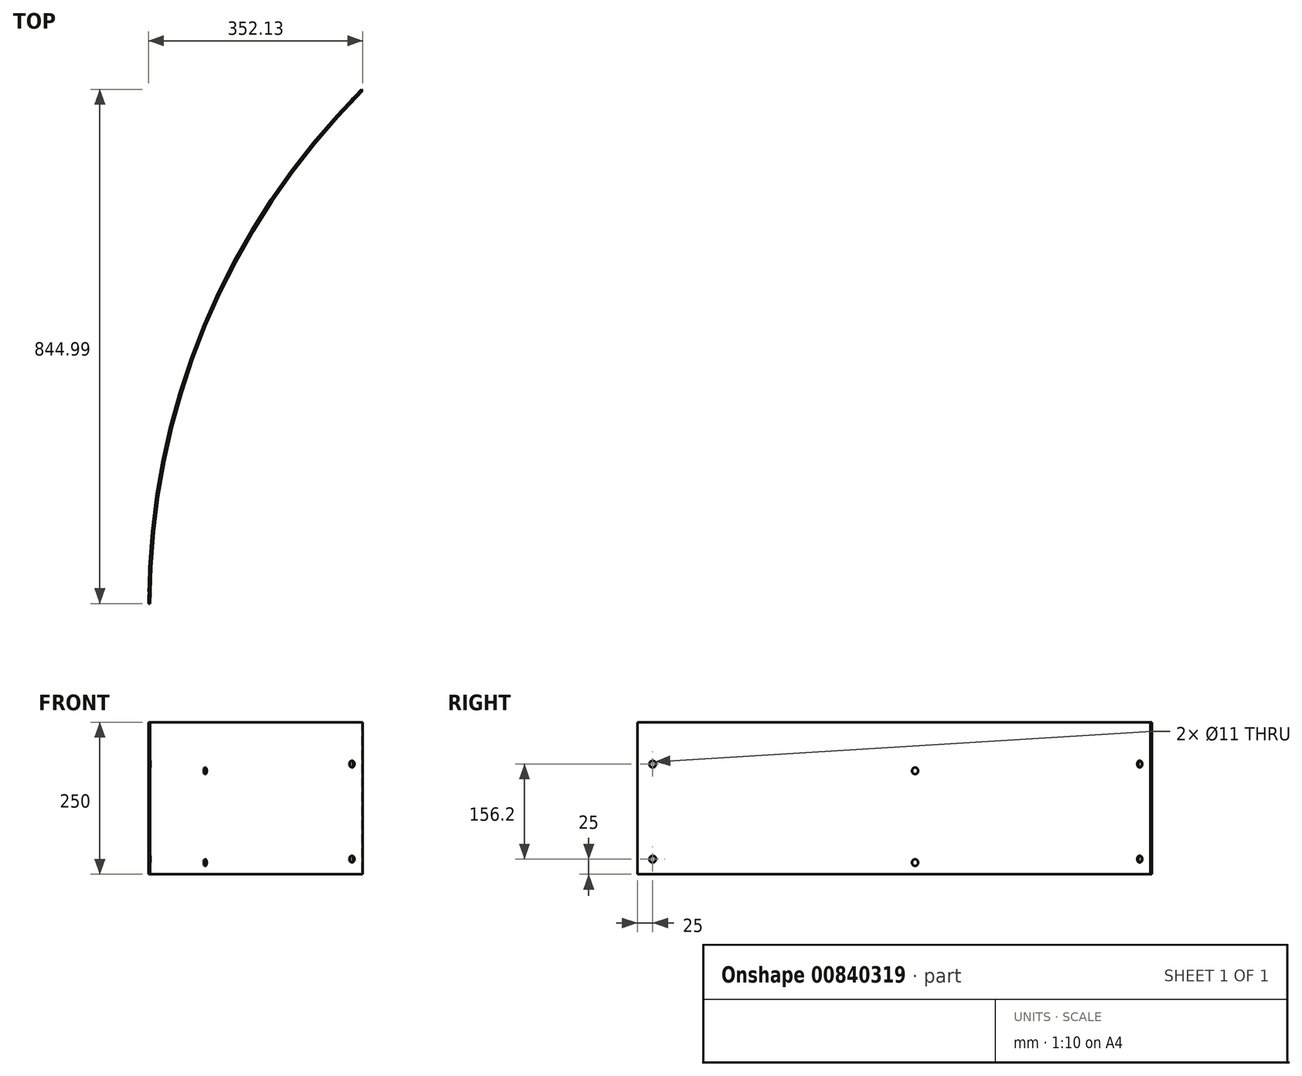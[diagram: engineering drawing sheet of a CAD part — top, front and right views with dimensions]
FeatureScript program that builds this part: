
annotation { "Feature Type Name" : "Feature", "Feature Type Description" : "" }
export const myFeature = defineFeature(function(context is Context, id is Id, definition is map)
    precondition{}
    {
        {
            var Q0;
            Q0=qCreatedBy(makeId("Top.planeOp"),FACE);
            var sketch = newSketch(context, id + "F0", { "sketchPlane" : qUnion([Q0])});
            skArc(sketch, "E0", {"start": v(349.13, 842.87) * mm, "mid": v(90.74, 456.16) * mm, "end": v(0, 0) * mm});
            skLineSegment(sketch, "E1", {"start": v(0, 0) * mm, "end": v(1192, 0) * mm, "construction": true});
            skLineSegment(sketch, "E2", {"start": v(1192, 0) * mm, "end": v(349.13, 842.87) * mm, "construction": true});
            skSolve(sketch);
        }
        {
            var Q0;
            Q0=qCreatedBy(makeId("Front.planeOp"),FACE);
            var sketch = newSketch(context, id + "F1", { "sketchPlane" : qUnion([Q0])});
            skLineSegment(sketch, "E3.bottom", {"start": v(0, 125) * mm, "end": v(-3, 125) * mm});
            skLineSegment(sketch, "E3.top", {"start": v(0, -125) * mm, "end": v(-3, -125) * mm});
            skLineSegment(sketch, "E3.left", {"start": v(0, 125) * mm, "end": v(0, -125) * mm});
            skLineSegment(sketch, "E3.right", {"start": v(-3, 125) * mm, "end": v(-3, -125) * mm});
            skSolve(sketch);
        }
        {
            var Q0;
            Q0=makeQuery(id+"F1.imprint","IMPRINT",FACE,{"disambiguationData":[TD([[makeQuery(id+"F1.imprint","IMPRINT",EDGE,{"derivedFrom":sQuery(id+"F1.wireOp",EDGE,"E3.bottom")}),1.0]])]});
            var Q1;
            Q1=sQuery(id+"F0.wireOp",EDGE,"A1xx75fL-8SPs-Z9ri-CPTb-JmtdQX2gj51n");
            var Q2;
            Q2=sQuery(id+"F0.wireOp",EDGE,"E0");
            var Q3;
            Q3=sQuery(id+"F0.wireOp",EDGE,"6DeDyjJt-B3l9-2hQ4-MW4A-s2AXSr22zXWG");
            sweep(context, id + "F2", {"profiles" : qUnion([Q0]), "path" : qUnion([Q1, Q2, Q3])});
        }
        {
            var Q0;
            Q0=qCreatedBy(makeId("Right.planeOp"),FACE);
            var sketch = newSketch(context, id + "F3", { "sketchPlane" : qUnion([Q0])});
            skPoint(sketch, "E4", {"position": v(25, -100) * mm});
            skPoint(sketch, "E5", {"position": v(25, 56.2) * mm});
            skCircle(sketch, "E6", {"center": v(25, 56.2) * mm, "radius": 5.5 * mm});
            skCircle(sketch, "E7", {"center": v(25, -100) * mm, "radius": 5.5 * mm});
            skSolve(sketch);
        }
        {
            var Q0;
            Q0=qSketchRegion(id+"F3",true);
            extrude(context, id + "F4", {"entities" : qUnion([Q0]), "operationType" : NewBodyOperationType.REMOVE, "endBound" : BoundingType.THROUGH_ALL, "depth" : 25 * mm, "offsetDistance" : 25 * mm, "hasSecondDirection" : true, "secondDirectionBound" : SecondDirectionBoundingType.THROUGH_ALL, "secondDirectionOppositeDirection" : true, "secondDirectionDepth" : 25 * mm});
        }
        {
            var Q0;
            Q0=qCreatedBy(makeId("Top.planeOp"),FACE);
            var sketch = newSketch(context, id + "F5", { "sketchPlane" : qUnion([Q0])});
            skLineSegment(sketch, "E8", {"start": v(0, 0) * mm, "end": v(353.55, 353.55) * mm, "construction": true});
            skSolve(sketch);
        }
        {
            var Q0;
            Q0=sQuery(id+"F5.wireOp",EDGE,"E8");
            var Q1;
            Q1=qCreatedBy(makeId("Right.planeOp"),FACE);
            cPlane(context, id + "F6", {"entities" : qUnion([Q0, Q1]), "cplaneType" : CPlaneType.LINE_ANGLE, "offset" : 25 * mm, "angle" : 0 * degree, "width" : 150 * mm, "height" : 150 * mm});
        }
        {
            var Q0;
            Q0=qCreatedBy(id+"F6.planeOp",FACE);
            var sketch = newSketch(context, id + "F7", { "sketchPlane" : qUnion([Q0])});
            skPoint(sketch, "E9", {"position": v(-817.87, -100) * mm});
            skPoint(sketch, "E10", {"position": v(-817.87, 56.2) * mm});
            skSolve(sketch);
        }
        {
            var Q0;
            Q0=sQuery(id+"F7.wireOp",VERTEX,"E10");
            var Q1;
            Q1=sQuery(id+"F7.wireOp",VERTEX,"E9");
            var Q2;
            Q2=makeQuery(id+"F2.opSweep","SWEPT_BODY",BODY,{"disambiguationData":[OSD([sQuery(id+"F0.wireOp",EDGE,"E0"),sQuery(id+"F1.wireOp",EDGE,"E3.bottom"),sQuery(id+"F1.wireOp",EDGE,"E3.top"),sQuery(id+"F1.wireOp",EDGE,"E3.left"),sQuery(id+"F1.wireOp",EDGE,"E3.right")])]});
            hole(context, id + "F8", {"style" : HoleStyle.SIMPLE, "endStyle" : HoleEndStyle.THROUGH, "oppositeDirection" : true, "standardTappedOrClearance" : lookupTablePath({ "fit" : "Normal", "standard" : "ISO", "size" : "M10", "type" : "Clearance" }), "standardBlindInLast" : lookupTablePath({ "fit" : "Standard", "standard" : "ISO", "size" : "M10", "type" : "Clearance" }), "holeDiameter" : 11 * mm, "majorDiameter" : 5 * mm, "isTappedThrough" : true, "tappedDepth" : 20 * mm, "tapClearance" : 3, "startFromSketch" : true, "locations" : qUnion([Q0, Q1]), "scope" : qUnion([Q2])});
        }
        {
            var Q0;
            Q0=makeQuery(id+"F2.opSweep","SWEPT_FACE",FACE,{"disambiguationData":[OSD([sQuery(id+"F0.wireOp",EDGE,"E0"),sQuery(id+"F1.wireOp",EDGE,"E3.bottom")])]});
            var sketch = newSketch(context, id + "F9", { "sketchPlane" : qUnion([Q0])});
            skPoint(sketch, "E11", {"position": v(90.74, 456.16) * mm});
            skSolve(sketch);
        }
        {
            var Q0;
            Q0=qCreatedBy(makeId("Top.planeOp"),FACE);
            var sketch = newSketch(context, id + "F10", { "sketchPlane" : qUnion([Q0])});
            skLineSegment(sketch, "E12", {"start": v(0, 0) * mm, "end": v(191.34, 461.94) * mm, "construction": true});
            skSolve(sketch);
        }
        {
            var Q0;
            Q0=sQuery(id+"F10.wireOp",EDGE,"E12");
            var Q1;
            Q1=qCreatedBy(makeId("Right.planeOp"),FACE);
            cPlane(context, id + "F11", {"entities" : qUnion([Q0, Q1]), "cplaneType" : CPlaneType.LINE_ANGLE, "offset" : 25 * mm, "angle" : 0 * degree, "width" : 150 * mm, "height" : 150 * mm});
        }
        {
            var Q0;
            Q0=qCreatedBy(id+"F11.planeOp",FACE);
            var sketch = newSketch(context, id + "F12", { "sketchPlane" : qUnion([Q0])});
            skPoint(sketch, "E13", {"position": v(-456.16, -105.7) * mm});
            skPoint(sketch, "E14", {"position": v(-456.16, 45.1) * mm});
            skLineSegment(sketch, "E15", {"start": v(-912.32, 0) * mm, "end": v(0, 0) * mm, "construction": true});
            skLineSegment(sketch, "E16", {"start": v(-456.16, 45.1) * mm, "end": v(-456.16, -105.7) * mm, "construction": true});
            skPoint(sketch, "E17", {"position": v(-456.16, 0) * mm});
            skSolve(sketch);
        }
        {
            var Q0;
            Q0=sQuery(id+"F12.wireOp",VERTEX,"E14");
            var Q1;
            Q1=sQuery(id+"F12.wireOp",VERTEX,"E13");
            var Q2;
            Q2=makeQuery(id+"F2.opSweep","SWEPT_BODY",BODY,{"disambiguationData":[OSD([sQuery(id+"F0.wireOp",EDGE,"E0"),sQuery(id+"F1.wireOp",EDGE,"E3.bottom"),sQuery(id+"F1.wireOp",EDGE,"E3.top"),sQuery(id+"F1.wireOp",EDGE,"E3.left"),sQuery(id+"F1.wireOp",EDGE,"E3.right")])]});
            hole(context, id + "F13", {"style" : HoleStyle.SIMPLE, "endStyle" : HoleEndStyle.THROUGH, "oppositeDirection" : true, "standardTappedOrClearance" : lookupTablePath({ "fit" : "Normal", "standard" : "ISO", "size" : "M10", "type" : "Clearance" }), "standardBlindInLast" : lookupTablePath({ "fit" : "Standard", "standard" : "ISO", "size" : "M10", "type" : "Clearance" }), "holeDiameter" : 11 * mm, "majorDiameter" : 10 * mm, "isTappedThrough" : true, "tappedDepth" : 20 * mm, "tapClearance" : 3, "startFromSketch" : true, "locations" : qUnion([Q0, Q1]), "scope" : qUnion([Q2])});
        }
    });
